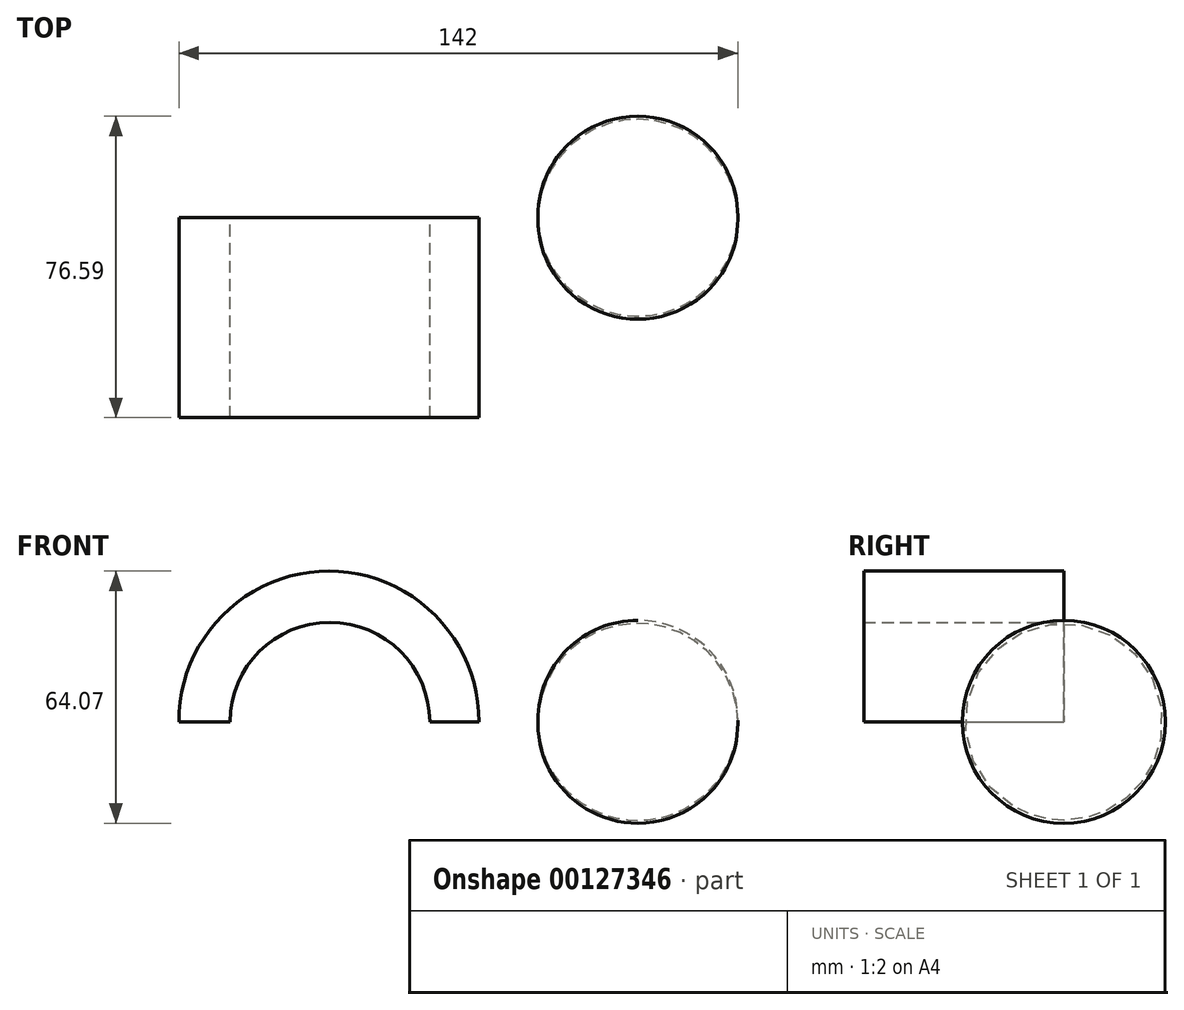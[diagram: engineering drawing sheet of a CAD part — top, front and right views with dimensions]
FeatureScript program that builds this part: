
annotation { "Feature Type Name" : "Feature", "Feature Type Description" : "" }
export const myFeature = defineFeature(function(context is Context, id is Id, definition is map)
    precondition{}
    {
        {
            var Q0;
            Q0=qCreatedBy(makeId("Front.planeOp"),FACE);
            var sketch = newSketch(context, id + "F0", { "sketchPlane" : qUnion([Q0])});
            skLineSegment(sketch, "E0", {"start": v(-25.7, 0) * mm, "end": v(25.1, 0) * mm});
            skArc(sketch, "E1", {"start": v(25.1, 0) * mm, "mid": v(-0.3, 25.01) * mm, "end": v(-25.7, 0) * mm});
            skSolve(sketch);
        }
        {
            var Q0;
            Q0 = qSketchRegion(id + "F0", true);
            var Q1;
            Q1=sQuery(id+"F0.wireOp",EDGE,"E0");
            revolve(context, id + "F1", {"entities" : qUnion([Q0]), "axis" : qUnion([Q1]), "revolveType" : RevolveType.FULL});
        }
        {
            var Q0;
            Q0=qCreatedBy(makeId("Front.planeOp"),FACE);
            var sketch = newSketch(context, id + "F2", { "sketchPlane" : qUnion([Q0])});
            skArc(sketch, "E2", {"start": v(-40.7, 0) * mm, "mid": v(-78.8, 38.28) * mm, "end": v(-116.9, 0) * mm});
            skLineSegment(sketch, "E3.trimOffspring", {"start": v(-53.16, 0) * mm, "end": v(-40.7, 0) * mm});
            skLineSegment(sketch, "E4", {"start": v(-103.96, 0) * mm, "end": v(-116.9, 0) * mm});
            skArc(sketch, "E5", {"start": v(-53.16, 0) * mm, "mid": v(-78.56, 25.29) * mm, "end": v(-103.96, 0) * mm});
            skLineSegment(sketch, "E6", {"start": v(-78.56, -0.11) * mm, "end": v(-78.56, 0) * mm});
            skPoint(sketch, "E7.orphan", {"position": v(-78.56, 25.29) * mm});
            skPoint(sketch, "E8.end.orphan", {"position": v(-78.8, 38.28) * mm});
            skSolve(sketch);
        }
        {
            var Q0;
            Q0 = qSketchRegion(id + "F2", true);
            extrude(context, id + "F3", {"entities" : qUnion([Q0]), "depth" : 50.8 * mm});
        }
    });
